# Revit family: Work_Tools_&_Leg_Screens-Teknion-CQCCS_Routes_Coat_Stand-R2018
name_source: partatom
category: Furniture
revit_build: Autodesk Revit 2018 (Build: 20170223_1515(x64)
units: mm (PartAtom-declared; Revit-internal decimal feet)

## family parameters
Always vertical = Yes
Cut with Voids When Loaded = No
OmniClass Number = 23.40.70.14.64.21
OmniClass Title = Systems Furniture
Room Calculation Point = No
Shared = Yes
Work Plane-Based = No

## types (1)
- Coat Stand
    Assembly Code = E2020200
    Description = Routes Coat Stand
    Manufacturer = Teknion
    Manufacturer Fax = 416.661.4586
    Model = CQCCS
    Part Number = CQCCS
    Product Documentation Link = https://assets.teknion.com
    Product Line = Routes
    Product Page URL = https://www.teknion.com
    Series = Routes
    Sustainability Data = http://www.teknion.com
    URL = www.teknion.com
    Warranty = http://www.teknion.com

## geometry (parser evidence)
native form markers: Sweep x2
no freeform markers — native parametric forms only
